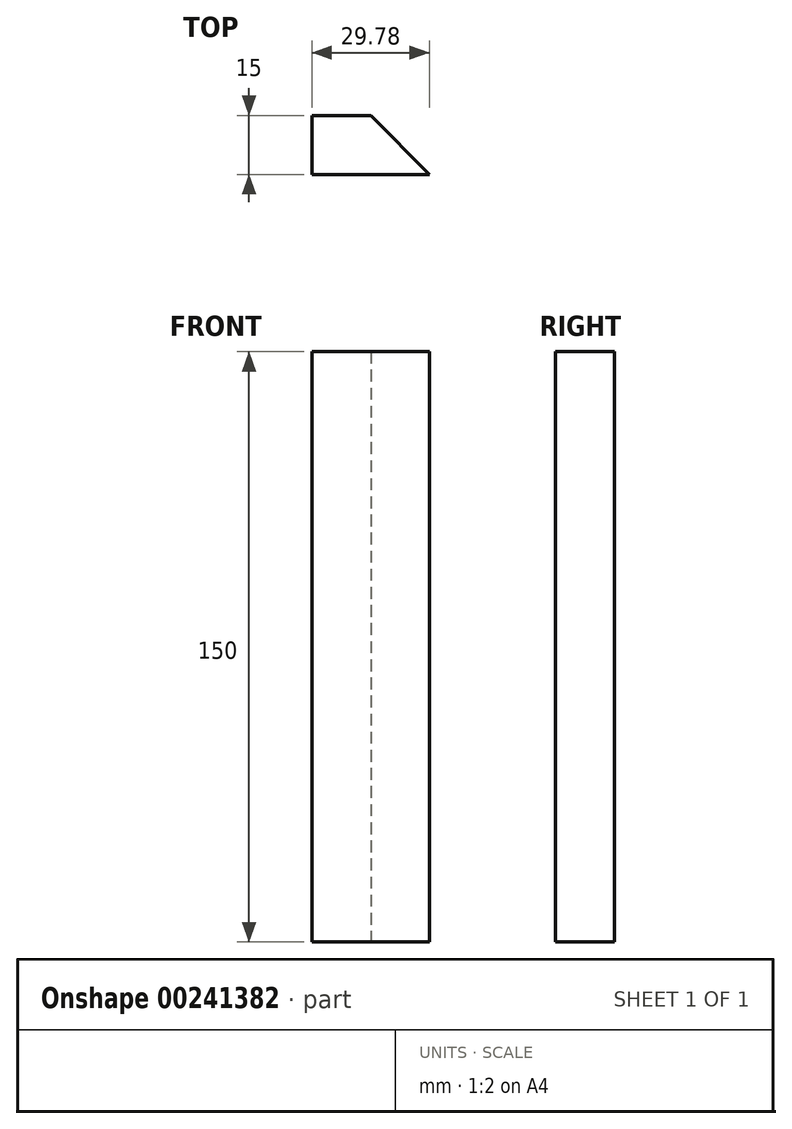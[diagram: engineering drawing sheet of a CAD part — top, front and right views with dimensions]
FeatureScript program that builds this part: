
annotation { "Feature Type Name" : "Feature", "Feature Type Description" : "" }
export const myFeature = defineFeature(function(context is Context, id is Id, definition is map)
    precondition{}
    {
        {
            var Q0;
            Q0=qCreatedBy(makeId("Top.planeOp"),FACE);
            var sketch = newSketch(context, id + "F0", { "sketchPlane" : qUnion([Q0])});
            skLineSegment(sketch, "E0", {"start": v(-7.5, -6.7) * mm, "end": v(-7.5, 8.3) * mm});
            skLineSegment(sketch, "E1", {"start": v(-7.5, 8.3) * mm, "end": v(7.5, 8.3) * mm});
            skLineSegment(sketch, "E2", {"start": v(7.5, 8.3) * mm, "end": v(22.28, -6.7) * mm});
            skLineSegment(sketch, "E3", {"start": v(22.28, -6.7) * mm, "end": v(-7.5, -6.7) * mm});
            skSolve(sketch);
        }
        {
            var Q0;
            Q0=qSketchRegion(id+"F0",true);
            extrude(context, id + "F1", {"entities" : qUnion([Q0]), "depth" : 150 * mm});
        }
    });
